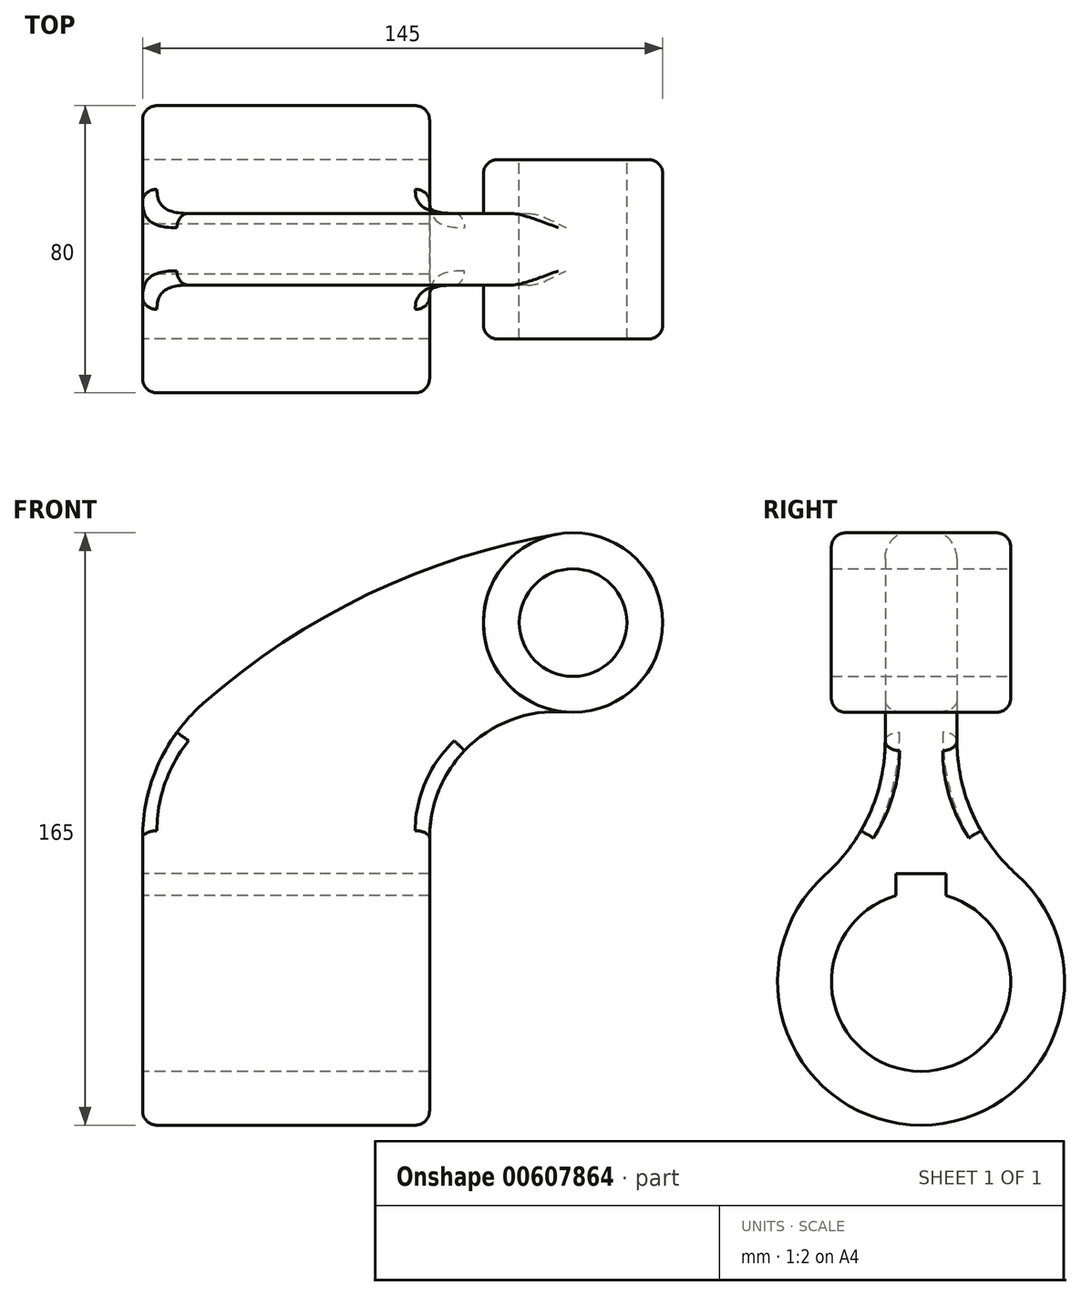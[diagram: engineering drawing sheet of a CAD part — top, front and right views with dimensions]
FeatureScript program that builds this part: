
annotation { "Feature Type Name" : "Feature", "Feature Type Description" : "" }
export const myFeature = defineFeature(function(context is Context, id is Id, definition is map)
    precondition{}
    {
        {
            var Q0;
            Q0=qCreatedBy(makeId("Front.planeOp"),FACE);
            var sketch = newSketch(context, id + "F0", { "sketchPlane" : qUnion([Q0])});
            skLineSegment(sketch, "E0", {"start": v(-14.88, 0) * mm, "end": v(96.43, 0) * mm, "construction": true});
            skLineSegment(sketch, "E1.bottom", {"start": v(0, 25) * mm, "end": v(80, 25) * mm});
            skLineSegment(sketch, "E1.top", {"start": v(0, 40) * mm, "end": v(80, 40) * mm});
            skLineSegment(sketch, "E1.left", {"start": v(0, 25) * mm, "end": v(0, 40) * mm});
            skLineSegment(sketch, "E1.right", {"start": v(80, 25) * mm, "end": v(80, 40) * mm});
            skCircle(sketch, "E2", {"center": v(120, 100) * mm, "radius": 15 * mm});
            skCircle(sketch, "E3", {"center": v(120, 100) * mm, "radius": 25 * mm});
            skArc(sketch, "E4", {"start": v(118, 75.08) * mm, "mid": v(91.32, 65.86) * mm, "end": v(80, 40) * mm});
            skArc(sketch, "E5", {"start": v(16.95, 77.52) * mm, "mid": v(4.43, 60.58) * mm, "end": v(0, 40) * mm});
            skArc(sketch, "E6", {"start": v(115.84, 124.65) * mm, "mid": v(63.1, 107.99) * mm, "end": v(16.95, 77.52) * mm});
            skSolve(sketch);
        }
        {
            var Q0;
            Q0=makeQuery(id+"F0.imprint","IMPRINT",FACE,{"disambiguationData":[TD([[makeQuery(id+"F0.imprint","IMPRINT",EDGE,{"derivedFrom":sQuery(id+"F0.wireOp",EDGE,"E1.bottom")}),1.0]])]});
            var Q1;
            Q1=sQuery(id+"F0.wireOp",EDGE,"E0");
            revolve(context, id + "F1", {"entities" : qUnion([Q0]), "axis" : qUnion([Q1]), "revolveType" : RevolveType.FULL});
        }
        {
            var Q0;
            Q0=makeQuery(id+"F0.imprint","IMPRINT",FACE,{"disambiguationData":[TD([[makeQuery(id+"F0.imprint","IMPRINT",EDGE,{"derivedFrom":sQuery(id+"F0.wireOp",EDGE,"E1.top")}),1.0]])]});
            var Q1;
            Q1=makeQuery(id+"F0.imprint","IMPRINT",FACE,{"disambiguationData":[TD([[makeQuery(id+"F0.imprint","IMPRINT",EDGE,{"derivedFrom":sQuery(id+"F0.wireOp",EDGE,"E1.bottom")}),1.0]])]});
            extrude(context, id + "F2", {"entities" : qUnion([Q0, Q1]), "operationType" : NewBodyOperationType.ADD, "endBound" : BoundingType.SYMMETRIC, "depth" : 20 * mm, "offsetDistance" : 25 * mm});
        }
        {
            var Q0;
            Q0=makeQuery(id+"F0.imprint","IMPRINT",FACE,{"disambiguationData":[TD([[makeQuery(id+"F0.imprint","IMPRINT",EDGE,{"derivedFrom":sQuery(id+"F0.wireOp",EDGE,"E2")}),-1.0]])]});
            extrude(context, id + "F3", {"entities" : qUnion([Q0]), "operationType" : NewBodyOperationType.ADD, "endBound" : BoundingType.SYMMETRIC, "depth" : 50 * mm, "offsetDistance" : 25 * mm});
        }
        {
            var Q0;
            Q0=makeQuery(id+"F2.boolean.opBoolean","INTERSECT",EDGE,{"derivedFrom":[makeQuery(id+"F1.opRevolve","SWEPT_FACE",FACE,{"disambiguationData":[OSD([sQuery(id+"F0.wireOp",EDGE,"E1.top")])]}),makeQuery(id+"F2.opExtrude","CAP_FACE",FACE,{"disambiguationData":[OSD([sQuery(id+"F0.wireOp",EDGE,"E1.bottom"),sQuery(id+"F0.wireOp",EDGE,"E1.left"),sQuery(id+"F0.wireOp",EDGE,"E1.right"),sQuery(id+"F0.wireOp",EDGE,"E3"),sQuery(id+"F0.wireOp",EDGE,"E4"),sQuery(id+"F0.wireOp",EDGE,"E5"),sQuery(id+"F0.wireOp",EDGE,"E6")])],"isStart":false})]});
            var Q1;
            Q1=makeQuery(id+"F2.boolean.opBoolean","INTERSECT",EDGE,{"derivedFrom":[makeQuery(id+"F1.opRevolve","SWEPT_FACE",FACE,{"disambiguationData":[OSD([sQuery(id+"F0.wireOp",EDGE,"E1.top")])]}),makeQuery(id+"F2.opExtrude","CAP_FACE",FACE,{"disambiguationData":[OSD([sQuery(id+"F0.wireOp",EDGE,"E1.bottom"),sQuery(id+"F0.wireOp",EDGE,"E1.left"),sQuery(id+"F0.wireOp",EDGE,"E1.right"),sQuery(id+"F0.wireOp",EDGE,"E3"),sQuery(id+"F0.wireOp",EDGE,"E4"),sQuery(id+"F0.wireOp",EDGE,"E5"),sQuery(id+"F0.wireOp",EDGE,"E6")])],"isStart":true})]});
            fillet(context, id + "F4", {"entities" : qUnion([Q0, Q1]), "radius" : 50 * mm, "tangentPropagation" : true, "allowEdgeOverflow" : false});
        }
        {
            var Q0;
            Q0=makeQuery(id+"F3.opExtrude","CAP_EDGE",EDGE,{"disambiguationData":[OSD([sQuery(id+"F0.wireOp",EDGE,"E3")])],"isStart":false});
            var Q1;
            Q1=makeQuery(id+"F3.opExtrude","CAP_EDGE",EDGE,{"disambiguationData":[OSD([sQuery(id+"F0.wireOp",EDGE,"E3")])],"isStart":true});
            var Q2;
            Q2=makeQuery(id+"F2.opExtrude","CAP_EDGE",EDGE,{"disambiguationData":[OSD([sQuery(id+"F0.wireOp",EDGE,"E6")])],"isStart":false});
            var Q3;
            Q3=makeQuery(id+"F2.opExtrude","CAP_EDGE",EDGE,{"disambiguationData":[OSD([sQuery(id+"F0.wireOp",EDGE,"E6")])],"isStart":true});
            var Q4;
            Q4=makeQuery(id+"F2.opExtrude","CAP_EDGE",EDGE,{"disambiguationData":[OSD([sQuery(id+"F0.wireOp",EDGE,"E5")])],"isStart":true});
            var Q5;
            {var subQ0=sQuery(id+"F0.wireOp",EDGE,"E4");Q5=makeQuery(id+"F4.opFillet","BLEND_EDGE",EDGE,{"blendedFrom":[makeQuery(id+"F2.boolean.opBoolean","INTERSECT",EDGE,{"derivedFrom":[makeQuery(id+"F1.opRevolve","SWEPT_FACE",FACE,{"disambiguationData":[OSD([sQuery(id+"F0.wireOp",EDGE,"E1.top")])]}),makeQuery(id+"F2.opExtrude","CAP_FACE",FACE,{"disambiguationData":[OSD([sQuery(id+"F0.wireOp",EDGE,"E1.bottom"),sQuery(id+"F0.wireOp",EDGE,"E1.left"),sQuery(id+"F0.wireOp",EDGE,"E1.right"),sQuery(id+"F0.wireOp",EDGE,"E3"),subQ0,sQuery(id+"F0.wireOp",EDGE,"E5"),sQuery(id+"F0.wireOp",EDGE,"E6")])],"isStart":true})]}),makeQuery(id+"F2.opExtrude","SWEPT_FACE",FACE,{"disambiguationData":[OSD([subQ0])]})],"blendedInto":[makeQuery(id+"F2.opExtrude","SWEPT_FACE",FACE,{"disambiguationData":[OSD([subQ0])]})]});}
            var Q6;
            {var subQ0=sQuery(id+"F0.wireOp",EDGE,"E4");Q6=makeQuery(id+"F4.opFillet","BLEND_EDGE",EDGE,{"blendedFrom":[makeQuery(id+"F2.boolean.opBoolean","INTERSECT",EDGE,{"derivedFrom":[makeQuery(id+"F1.opRevolve","SWEPT_FACE",FACE,{"disambiguationData":[OSD([sQuery(id+"F0.wireOp",EDGE,"E1.top")])]}),makeQuery(id+"F2.opExtrude","CAP_FACE",FACE,{"disambiguationData":[OSD([sQuery(id+"F0.wireOp",EDGE,"E1.bottom"),sQuery(id+"F0.wireOp",EDGE,"E1.left"),sQuery(id+"F0.wireOp",EDGE,"E1.right"),sQuery(id+"F0.wireOp",EDGE,"E3"),subQ0,sQuery(id+"F0.wireOp",EDGE,"E5"),sQuery(id+"F0.wireOp",EDGE,"E6")])],"isStart":false})]}),makeQuery(id+"F2.opExtrude","SWEPT_FACE",FACE,{"disambiguationData":[OSD([subQ0])]})],"blendedInto":[makeQuery(id+"F2.opExtrude","SWEPT_FACE",FACE,{"disambiguationData":[OSD([subQ0])]})]});}
            var Q7;
            Q7=makeQuery(id+"F2.opExtrude","CAP_EDGE",EDGE,{"disambiguationData":[OSD([sQuery(id+"F0.wireOp",EDGE,"E3")])],"isStart":true});
            var Q8;
            Q8=makeQuery(id+"F2.opExtrude","CAP_EDGE",EDGE,{"disambiguationData":[OSD([sQuery(id+"F0.wireOp",EDGE,"E3")])],"isStart":false});
            fillet(context, id + "F5", {"entities" : qUnion([Q0, Q1, Q2, Q3, Q4, Q5, Q6, Q7, Q8]), "radius" : 4 * mm, "tangentPropagation" : true, "allowEdgeOverflow" : false});
        }
        {
            var Q0;
            {var subQ0=sQuery(id+"F0.wireOp",EDGE,"E1.left");Q0=makeQuery(id+"F2.boolean.opBoolean","MERGE",FACE,{"derivedFrom":[makeQuery(id+"F1.opRevolve","SWEPT_FACE",FACE,{"disambiguationData":[OSD([subQ0])]}),makeQuery(id+"F2.opExtrude","SWEPT_FACE",FACE,{"disambiguationData":[OSD([subQ0])]})]});}
            var sketch = newSketch(context, id + "F6", { "sketchPlane" : qUnion([Q0])});
            skLineSegment(sketch, "E7.bottom", {"start": v(-7, 30) * mm, "end": v(7, 30) * mm});
            skLineSegment(sketch, "E7.top", {"start": v(-7, 0) * mm, "end": v(7, 0) * mm});
            skLineSegment(sketch, "E7.left", {"start": v(-7, 30) * mm, "end": v(-7, 0) * mm});
            skLineSegment(sketch, "E7.right", {"start": v(7, 30) * mm, "end": v(7, 0) * mm});
            skSolve(sketch);
        }
        {
            var Q0;
            {var subQ0=sQuery(id+"F6.wireOp",EDGE,"E7.bottom");Q0=makeQuery(id+"F6.imprint","IMPRINT",FACE,{"disambiguationData":[TD([[makeQuery(id+"F6.imprint","IMPRINT",EDGE,{"derivedFrom":subQ0}),-1.0]])]});}
            extrude(context, id + "F7", {"entities" : qUnion([Q0]), "operationType" : NewBodyOperationType.REMOVE, "oppositeDirection" : true, "depth" : 80 * mm, "offsetDistance" : 25 * mm});
        }
    });
